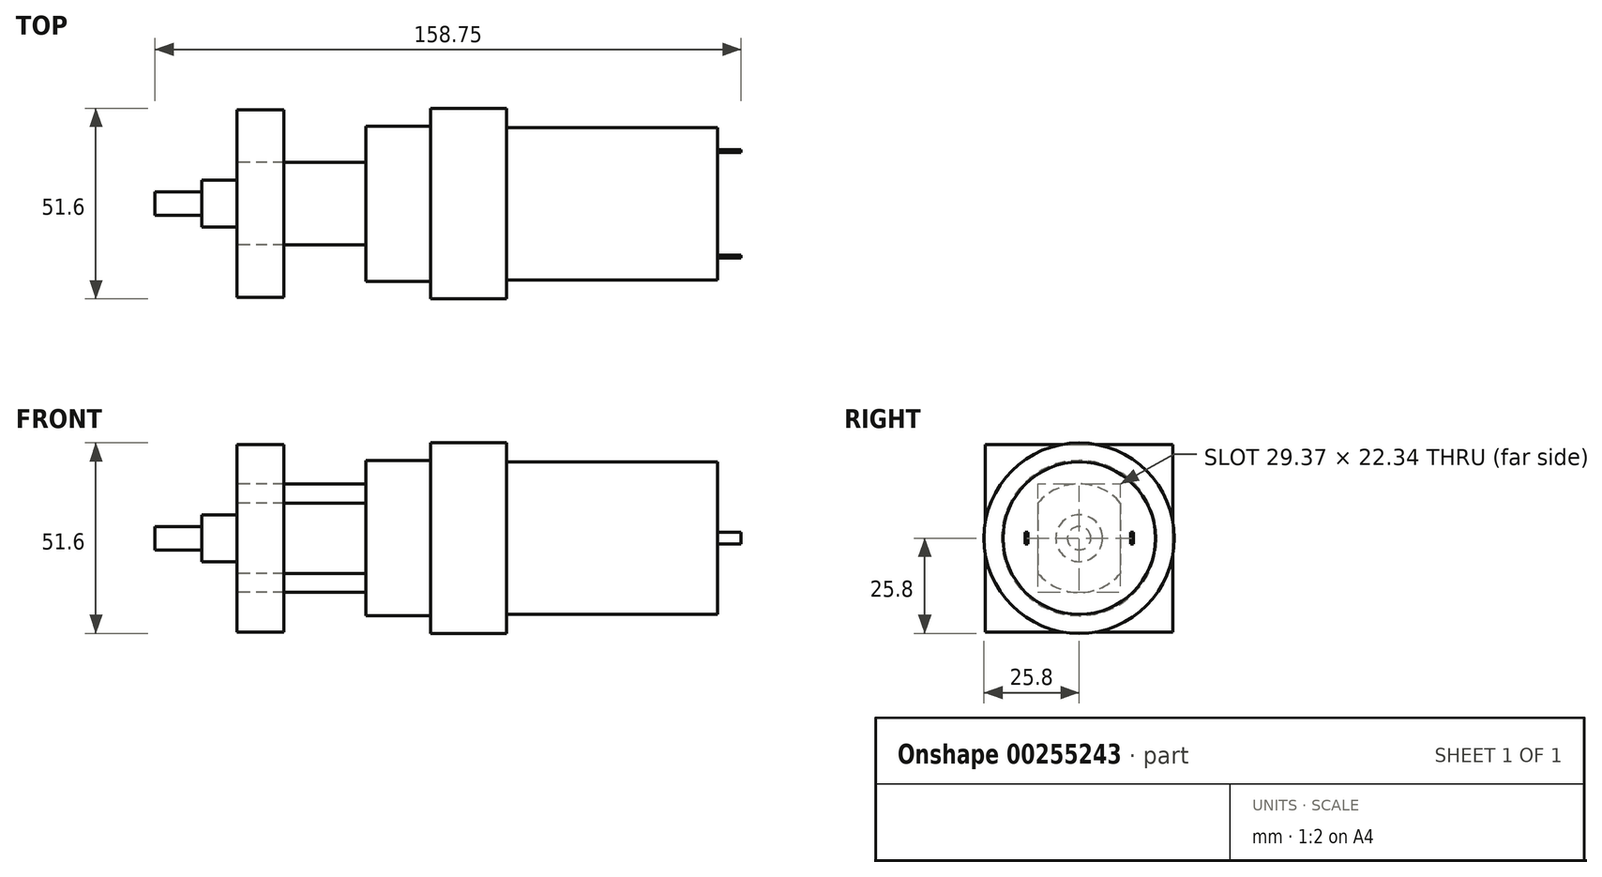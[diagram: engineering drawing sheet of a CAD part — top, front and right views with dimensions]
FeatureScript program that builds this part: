
annotation { "Feature Type Name" : "Feature", "Feature Type Description" : "" }
export const myFeature = defineFeature(function(context is Context, id is Id, definition is map)
    precondition{}
    {
        {
            var Q0;
            Q0=qCreatedBy(makeId("Top.planeOp"),FACE);
            var sketch = newSketch(context, id + "F0", { "sketchPlane" : qUnion([Q0])});
            skLineSegment(sketch, "E0", {"start": v(0, 0) * mm, "end": v(-107.34, 0) * mm, "construction": true});
            skLineSegment(sketch, "E1", {"start": v(0, 0) * mm, "end": v(0, 20.64) * mm});
            skLineSegment(sketch, "E2", {"start": v(0, 20.64) * mm, "end": v(-57.15, 20.64) * mm});
            skLineSegment(sketch, "E3", {"start": v(-57.15, 20.64) * mm, "end": v(-57.15, 25.8) * mm});
            skLineSegment(sketch, "E4", {"start": v(-57.15, 25.8) * mm, "end": v(-77.79, 25.8) * mm});
            skLineSegment(sketch, "E5", {"start": v(-77.79, 25.8) * mm, "end": v(-77.79, 21.03) * mm});
            skLineSegment(sketch, "E6", {"start": v(-77.79, 21.03) * mm, "end": v(-95.25, 21.03) * mm});
            skLineSegment(sketch, "E7", {"start": v(-95.25, 21.03) * mm, "end": v(-95.25, 14.68) * mm});
            skLineSegment(sketch, "E8", {"start": v(-95.25, 14.68) * mm, "end": v(-130.18, 14.68) * mm});
            skLineSegment(sketch, "E9", {"start": v(-130.18, 14.68) * mm, "end": v(-130.18, 6.35) * mm});
            skLineSegment(sketch, "E10", {"start": v(-130.18, 6.35) * mm, "end": v(-139.7, 6.35) * mm});
            skLineSegment(sketch, "E11", {"start": v(-139.7, 6.35) * mm, "end": v(-139.7, 3.17) * mm});
            skLineSegment(sketch, "E12", {"start": v(-139.7, 3.17) * mm, "end": v(-152.4, 3.17) * mm});
            skLineSegment(sketch, "E13", {"start": v(-152.4, 3.17) * mm, "end": v(-152.4, 0) * mm});
            skLineSegment(sketch, "E14", {"start": v(-57.15, 20.64) * mm, "end": v(-57.15, 0) * mm});
            skLineSegment(sketch, "E15", {"start": v(-57.15, 0) * mm, "end": v(0, 0) * mm});
            skLineSegment(sketch, "E16", {"start": v(-152.4, 0) * mm, "end": v(-57.15, 0) * mm});
            skLineSegment(sketch, "E17", {"start": v(-139.7, 3.17) * mm, "end": v(-139.7, 0) * mm});
            skLineSegment(sketch, "E18", {"start": v(-130.18, 6.35) * mm, "end": v(-130.18, 0) * mm});
            skSolve(sketch);
        }
        {
            var Q0;
            Q0=makeQuery(id+"F0.imprint","IMPRINT",FACE,{"disambiguationData":[TD([[makeQuery(id+"F0.imprint","IMPRINT",EDGE,{"derivedFrom":sQuery(id+"F0.wireOp",EDGE,"E3")}),1.0]])]});
            var Q1;
            Q1=sQuery(id+"F0.wireOp",EDGE,"E16");
            revolve(context, id + "F1", {"entities" : qUnion([Q0]), "axis" : qUnion([Q1]), "revolveType" : RevolveType.FULL});
        }
        {
            var Q0;
            Q0=makeQuery(id+"F0.imprint","IMPRINT",FACE,{"disambiguationData":[TD([[makeQuery(id+"F0.imprint","IMPRINT",EDGE,{"derivedFrom":sQuery(id+"F0.wireOp",EDGE,"E1")}),1.0]])]});
            var Q1;
            Q1=sQuery(id+"F0.wireOp",EDGE,"E15");
            revolve(context, id + "F2", {"entities" : qUnion([Q0]), "axis" : qUnion([Q1]), "revolveType" : RevolveType.FULL});
        }
        {
            var Q0;
            Q0=makeQuery(id+"F0.imprint","IMPRINT",FACE,{"disambiguationData":[TD([[makeQuery(id+"F0.imprint","IMPRINT",EDGE,{"derivedFrom":sQuery(id+"F0.wireOp",EDGE,"E10")}),1.0]])]});
            var Q1;
            Q1=sQuery(id+"F0.wireOp",EDGE,"E16");
            revolve(context, id + "F3", {"entities" : qUnion([Q0]), "axis" : qUnion([Q1]), "revolveType" : RevolveType.FULL});
        }
        {
            var Q0;
            Q0=makeQuery(id+"F0.imprint","IMPRINT",FACE,{"disambiguationData":[TD([[makeQuery(id+"F0.imprint","IMPRINT",EDGE,{"derivedFrom":sQuery(id+"F0.wireOp",EDGE,"E12")}),1.0]])]});
            var Q1;
            Q1=sQuery(id+"F0.wireOp",EDGE,"E16");
            revolve(context, id + "F4", {"entities" : qUnion([Q0]), "axis" : qUnion([Q1]), "revolveType" : RevolveType.FULL});
        }
        {
            var Q0;
            Q0=makeQuery(id+"F1.opRevolve","SWEPT_FACE",FACE,{"disambiguationData":[OSD([sQuery(id+"F0.wireOp",EDGE,"E9"),sQuery(id+"F0.wireOp",EDGE,"E18")])]});
            var sketch = newSketch(context, id + "F5", { "sketchPlane" : qUnion([Q0])});
            skLineSegment(sketch, "E19.0", {"start": v(-25.8, 0) * mm, "end": v(-21.03, 0) * mm});
            skLineSegment(sketch, "E19.1", {"start": v(-21.03, 0) * mm, "end": v(-14.68, 0) * mm});
            skLineSegment(sketch, "E19.2", {"start": v(-14.68, 0) * mm, "end": v(-6.35, 0) * mm});
            skLineSegment(sketch, "E19.3", {"start": v(-6.35, 0) * mm, "end": v(0, 0) * mm});
            skLineSegment(sketch, "E20", {"start": v(-25.8, 0) * mm, "end": v(25.8, 0) * mm, "construction": true});
            skLineSegment(sketch, "E21.bottom", {"start": v(-14.98, 14.76) * mm, "end": v(-11.17, 14.76) * mm});
            skLineSegment(sketch, "E21.top", {"start": v(-14.98, -14.76) * mm, "end": v(-11.17, -14.76) * mm});
            skLineSegment(sketch, "E21.left", {"start": v(-14.98, 14.76) * mm, "end": v(-14.98, -14.76) * mm});
            skLineSegment(sketch, "E21.right", {"start": v(-11.17, 14.76) * mm, "end": v(-11.17, -14.76) * mm});
            skLineSegment(sketch, "E22", {"start": v(0, 25.9) * mm, "end": v(0, -25.83) * mm, "construction": true});
            skLineSegment(sketch, "E23.MirrorCS", {"start": v(14.98, 14.76) * mm, "end": v(14.98, -14.76) * mm});
            skLineSegment(sketch, "E24.MirrorCS", {"start": v(14.98, 14.76) * mm, "end": v(11.17, 14.76) * mm});
            skLineSegment(sketch, "E25.MirrorCS", {"start": v(11.17, 14.76) * mm, "end": v(11.17, -14.76) * mm});
            skLineSegment(sketch, "E26.MirrorCS", {"start": v(14.98, -14.76) * mm, "end": v(11.17, -14.76) * mm});
            skSolve(sketch);
        }
        {
            var Q0;
            {var subQ0=sQuery(id+"F5.wireOp",EDGE,"E19.2");var subQ3=sQuery(id+"F5.wireOp",EDGE,"E21.right");var subQ4=makeQuery(id+"F5.imprint","INTERSECT",VERTEX,{"derivedFrom":[subQ0,subQ3]});Q0=makeQuery(id+"F5.imprint","IMPRINT",FACE,{"disambiguationData":[TD([[makeQuery(id+"F5.imprint","IMPRINT",EDGE,{"disambiguationData":[TD([[subQ4,-1.0]])],"derivedFrom":subQ3}),-1.0]])]});}
            var Q1;
            {var subQ0=sQuery(id+"F5.wireOp",EDGE,"E19.2");var subQ3=sQuery(id+"F5.wireOp",EDGE,"E21.right");var subQ4=makeQuery(id+"F5.imprint","INTERSECT",VERTEX,{"derivedFrom":[subQ0,subQ3]});Q1=makeQuery(id+"F5.imprint","IMPRINT",FACE,{"disambiguationData":[TD([[makeQuery(id+"F5.imprint","IMPRINT",EDGE,{"disambiguationData":[TD([[subQ4,1.0]])],"derivedFrom":subQ3}),-1.0]])]});}
            var Q2;
            {var subQ0=sQuery(id+"F5.wireOp",EDGE,"E25.MirrorCS");var subQ1=makeQuery(id+"F1.opRevolve","SWEPT_EDGE",EDGE,{"disambiguationData":[OSD([sQuery(id+"F0.wireOp",EDGE,"E8"),sQuery(id+"F0.wireOp",EDGE,"E9")])]});var subQ2=makeQuery(id+"F5.imprint","INTERSECT",VERTEX,{"disambiguationData":[OD(0.0)],"derivedFrom":[subQ1,subQ0]});Q2=makeQuery(id+"F5.imprint","IMPRINT",FACE,{"disambiguationData":[TD([[makeQuery(id+"F5.imprint","IMPRINT",EDGE,{"disambiguationData":[TD([[subQ2,-1.0]])],"derivedFrom":subQ0}),1.0]])]});}
            var Q3;
            Q3=makeQuery(id+"F1.opRevolve","SWEPT_FACE",FACE,{"disambiguationData":[OSD([sQuery(id+"F0.wireOp",EDGE,"E7")])]});
            extrude(context, id + "F6", {"entities" : qUnion([Q0, Q1, Q2]), "operationType" : NewBodyOperationType.REMOVE, "endBound" : BoundingType.UP_TO_SURFACE, "oppositeDirection" : true, "endBoundEntityFace" : qUnion([Q3]), "depth" : 25.4 * mm});
        }
        {
            var Q0;
            Q0=makeQuery(id+"F2.opRevolve","SWEPT_FACE",FACE,{"disambiguationData":[OSD([sQuery(id+"F0.wireOp",EDGE,"E1")])]});
            var sketch = newSketch(context, id + "F7", { "sketchPlane" : qUnion([Q0])});
            skLineSegment(sketch, "E27.bottom", {"start": v(-13.9, -1.59) * mm, "end": v(-14.68, -1.59) * mm});
            skLineSegment(sketch, "E27.top", {"start": v(-13.9, 1.59) * mm, "end": v(-14.68, 1.59) * mm});
            skLineSegment(sketch, "E27.left", {"start": v(-13.9, -1.59) * mm, "end": v(-13.9, 1.59) * mm});
            skLineSegment(sketch, "E27.right", {"start": v(-14.68, -1.59) * mm, "end": v(-14.68, 1.59) * mm});
            skPoint(sketch, "E27.middle", {"position": v(-14.29, 0) * mm});
            skLineSegment(sketch, "E28", {"start": v(0, 20.64) * mm, "end": v(0, -20.64) * mm, "construction": true});
            skLineSegment(sketch, "E29.MirrorCS", {"start": v(14.68, -1.59) * mm, "end": v(14.68, 1.59) * mm});
            skLineSegment(sketch, "E30.MirrorCS", {"start": v(13.9, 1.59) * mm, "end": v(14.68, 1.59) * mm});
            skLineSegment(sketch, "E31.MirrorCS", {"start": v(13.9, -1.59) * mm, "end": v(13.9, 1.59) * mm});
            skLineSegment(sketch, "E32.MirrorCS", {"start": v(13.9, -1.59) * mm, "end": v(14.68, -1.59) * mm});
            skSolve(sketch);
        }
        {
            var Q0;
            Q0=qSketchRegion(id+"F7",true);
            extrude(context, id + "F8", {"entities" : qUnion([Q0]), "operationType" : NewBodyOperationType.ADD, "depth" : 6.35 * mm});
        }
        {
            var Q0;
            Q0=makeQuery(id+"F1.opRevolve","SWEPT_FACE",FACE,{"disambiguationData":[OSD([sQuery(id+"F0.wireOp",EDGE,"E9"),sQuery(id+"F0.wireOp",EDGE,"E18")])]});
            var sketch = newSketch(context, id + "F9", { "sketchPlane" : qUnion([Q0])});
            skLineSegment(sketch, "E33.bottom", {"start": v(25.4, -25.4) * mm, "end": v(-25.4, -25.4) * mm});
            skLineSegment(sketch, "E33.top", {"start": v(25.4, 25.4) * mm, "end": v(-25.4, 25.4) * mm});
            skLineSegment(sketch, "E33.left", {"start": v(25.4, -25.4) * mm, "end": v(25.4, 25.4) * mm});
            skLineSegment(sketch, "E33.right", {"start": v(-25.4, -25.4) * mm, "end": v(-25.4, 25.4) * mm});
            skPoint(sketch, "E33.middle", {"position": v(0, 0) * mm});
            skSolve(sketch);
        }
        {
            var Q0;
            Q0=makeQuery(id+"F9.imprint","IMPRINT",FACE,{"disambiguationData":[TD([[makeQuery(id+"F9.imprint","IMPRINT",EDGE,{"derivedFrom":sQuery(id+"F9.wireOp",EDGE,"E33.bottom")}),-1.0]])]});
            extrude(context, id + "F10", {"entities" : qUnion([Q0]), "oppositeDirection" : true, "depth" : 12.7 * mm});
        }
    });
